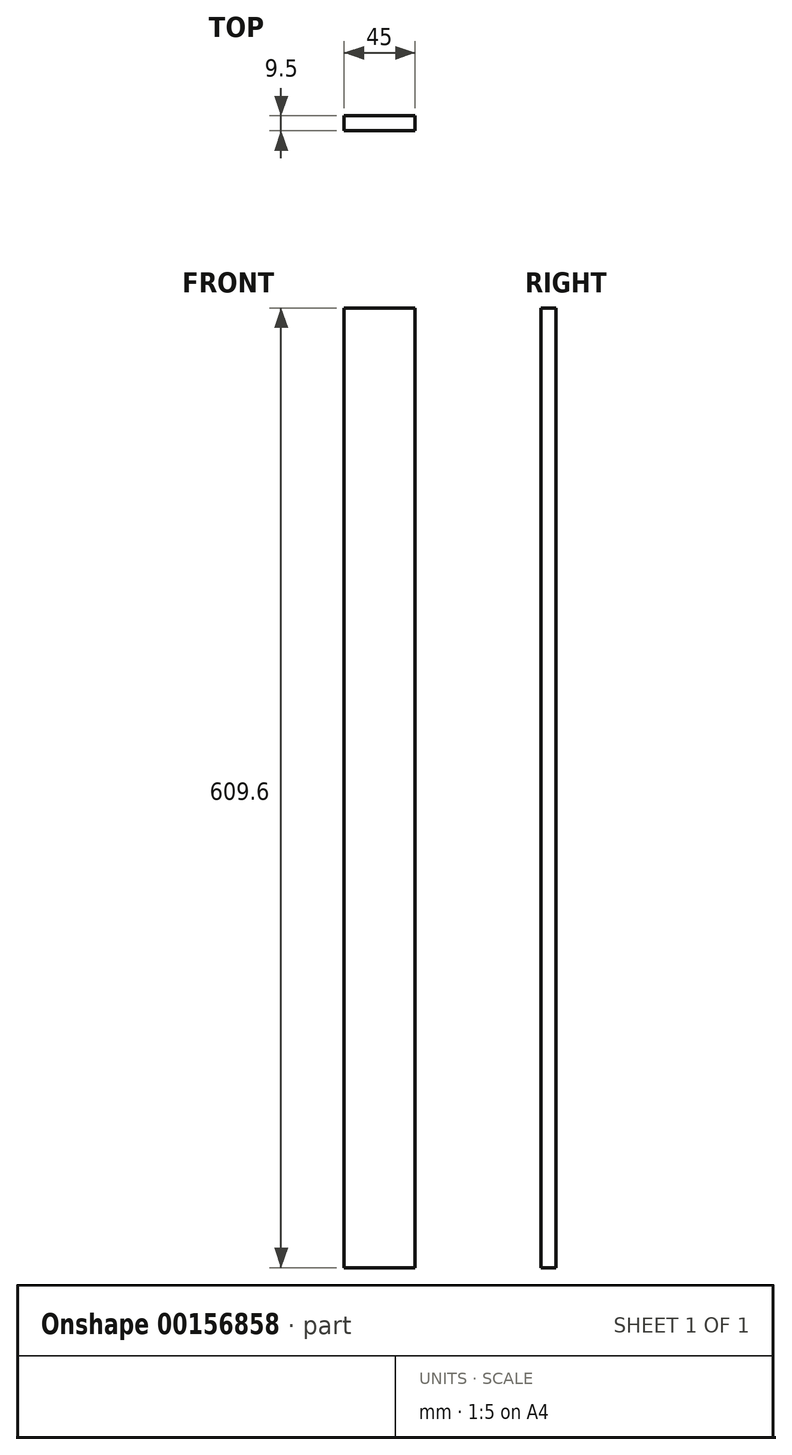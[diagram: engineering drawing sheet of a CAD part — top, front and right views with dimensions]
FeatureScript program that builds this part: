
annotation { "Feature Type Name" : "Feature", "Feature Type Description" : "" }
export const myFeature = defineFeature(function(context is Context, id is Id, definition is map)
    precondition{}
    {
        {
            var Q0;
            Q0=qCreatedBy(makeId("Top.planeOp"),FACE);
            var sketch = newSketch(context, id + "F0", { "sketchPlane" : qUnion([Q0])});
            skLineSegment(sketch, "E0.bottom", {"start": v(-22.5, -4.75) * mm, "end": v(22.5, -4.75) * mm});
            skLineSegment(sketch, "E0.top", {"start": v(-22.5, 4.75) * mm, "end": v(22.5, 4.75) * mm});
            skLineSegment(sketch, "E0.left", {"start": v(-22.5, -4.75) * mm, "end": v(-22.5, 4.75) * mm});
            skLineSegment(sketch, "E0.right", {"start": v(22.5, -4.75) * mm, "end": v(22.5, 4.75) * mm});
            skPoint(sketch, "E0.middle", {"position": v(0, 0) * mm});
            skSolve(sketch);
        }
        {
            var Q0;
            Q0 = qSketchRegion(id + "F0", true);
            extrude(context, id + "F1", {"entities" : qUnion([Q0]), "depth" : 609.6 * mm});
        }
    });
